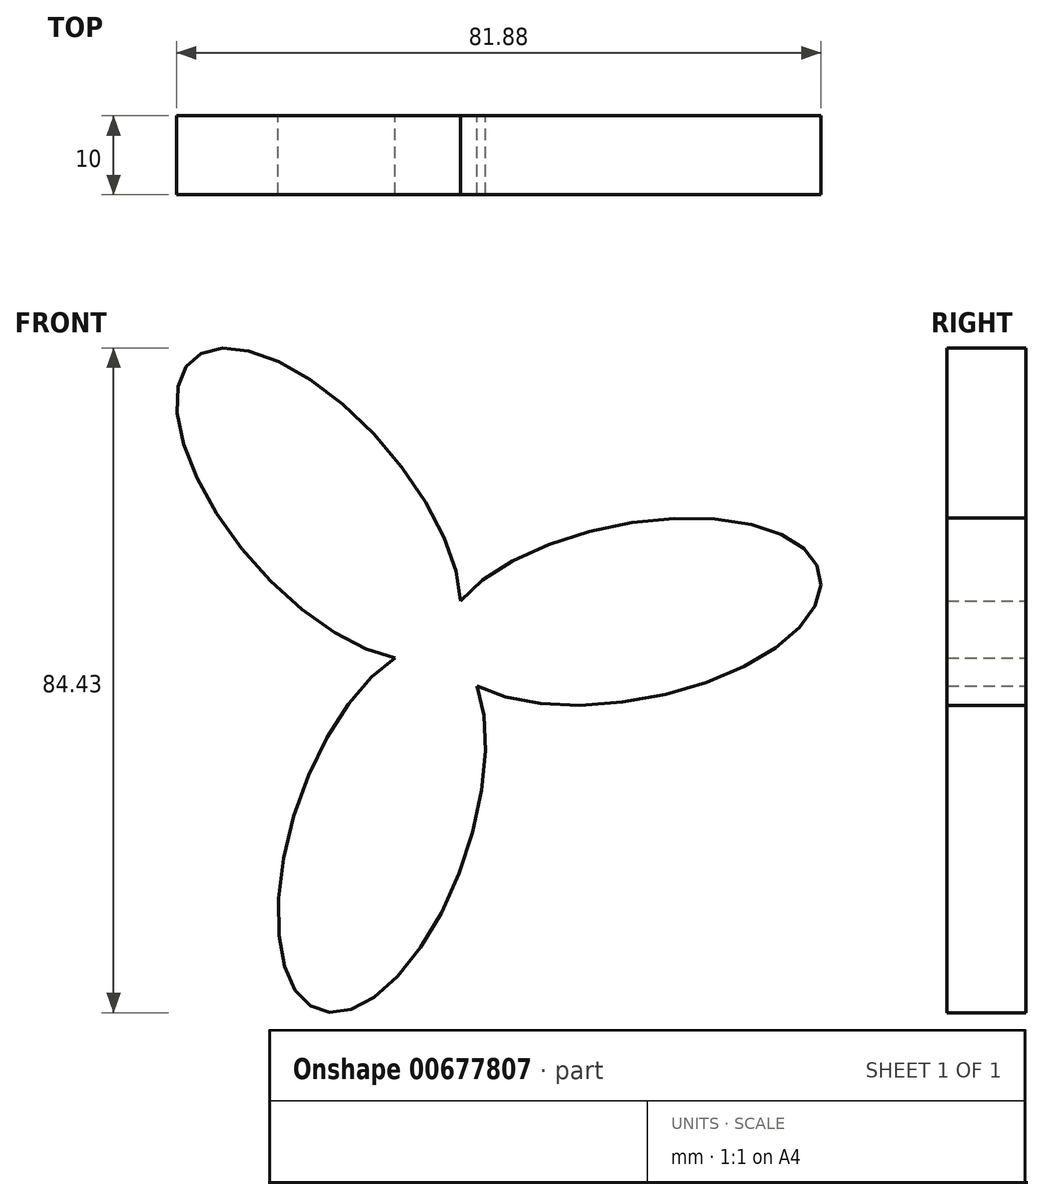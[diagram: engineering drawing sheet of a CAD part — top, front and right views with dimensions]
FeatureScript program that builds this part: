
annotation { "Feature Type Name" : "Feature", "Feature Type Description" : "" }
export const myFeature = defineFeature(function(context is Context, id is Id, definition is map)
    precondition{}
    {
        {
            var Q0;
            Q0=qCreatedBy(makeId("Front.planeOp"),FACE);
            var sketch = newSketch(context, id + "F0", { "sketchPlane" : qUnion([Q0])});
            skPoint(sketch, "E0.center", {"position": v(0, 0) * mm});
            skEllipse(sketch, "E1", {"center": v(-15.96, 18.37) * mm, "majorRadius": 24.33 * mm, "minorRadius": 11.15 * mm, "majorAxis": v(0.66, -0.75)});
            skEllipse(sketch, "E2.1.0", {"center": v(-7.92, -23) * mm, "majorRadius": 24.33 * mm, "minorRadius": 11.15 * mm, "majorAxis": v(0.33, 0.95)});
            skEllipse(sketch, "E2.2.0", {"center": v(23.89, 4.64) * mm, "majorRadius": 24.33 * mm, "minorRadius": 11.15 * mm, "majorAxis": v(-0.98, -0.2)});
            skSolve(sketch);
        }
        {
            var Q0;
            Q0 = qSketchRegion(id + "F0", true);
            extrude(context, id + "F1", {"entities" : qUnion([Q0]), "depth" : 5 * mm, "offsetDistance" : 25.4 * mm, "hasSecondDirection" : true, "secondDirectionOppositeDirection" : true, "secondDirectionDepth" : 5 * mm});
        }
    });
